# Revit family: xToilet-Elongated-Right_Height-American_Standard-Townsend-2922A_Series
name_source: partatom
category: Plumbing Fixtures
revit_build: Autodesk Revit 2014 (Build: 20130308_1515(x64)
units: mm (PartAtom-declared; Revit-internal decimal feet)

## types (2) — shared parameters
ADA Compliant = Yes
Assembly Code = D2010110
Bowl Shape = Elongated
CW Connection = Yes
CWFU = 5
Cold Water Connection Diameter = 1/2"
Cold Water Connection Height = 8"
Cold Water Connection Radius = 1/4"
Cold Water Connection Width = 6"
Default Elevation = 0"
Flush Rate = 1.28Gpf (4.8Lpf)
HW Connection = No
Height = 29 3/4"
Installation Type = Floor Mounted
Length = 30 3/16"
Manufacturer = American Standard
Material = Vitreous China-American Standard-020-White
Price = Prices may vary. Please consult Manufacturer Representative for most up-to-date price list.
URL = http://www.americanstandard-us.com
Vent Connection = No
WFU = 5
Warranty Information = 10 Year Limited
Waste Connection = Yes
Waste Connection Diameter = 2"
Waste Connection Radius = 1"
Width = 16 7/8"
zero-valued in all types: HWFU

## per-type parameters (varying)
| type | Description | Left Lever | Right Lever |
| 2922A.104 | Townsend Vormax Right Height Elongated One-Piece Toilet With Seat | Yes | No |
| 2922A.105 | Townsend Vormax Right Height Elongated One-Piece Toilet With Seat and Right Hand Trip Lever | No | Yes |

note: column(s) folded — value = type name in every type: Model

## geometry (parser evidence)
native form markers: Sweep x2
no freeform markers — native parametric forms only
